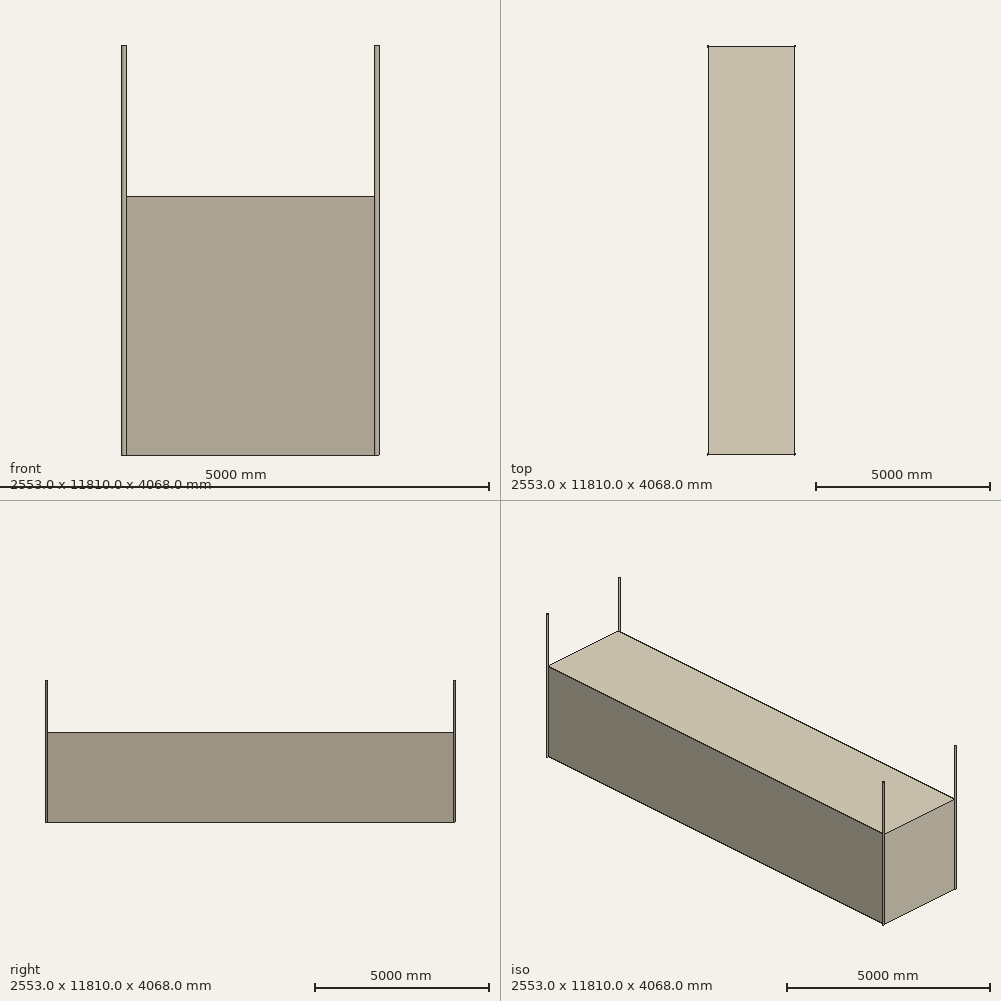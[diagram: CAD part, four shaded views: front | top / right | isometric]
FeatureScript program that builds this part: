
annotation { "Feature Type Name" : "Feature", "Feature Type Description" : "" }
export const myFeature = defineFeature(function(context is Context, id is Id, definition is map)
    precondition{}
    {
        {
            var Q0;
            Q0=qCreatedBy(makeId("Front.planeOp"),FACE);
            var sketch = newSketch(context, id + "F0", { "sketchPlane" : qUnion([Q0])});
            skLineSegment(sketch, "E0.bottom", {"start": v(-1226.5, 1284) * mm, "end": v(1226.5, 1284) * mm});
            skLineSegment(sketch, "E0.top", {"start": v(-1226.5, -1284) * mm, "end": v(1226.5, -1284) * mm});
            skLineSegment(sketch, "E0.left", {"start": v(-1226.5, 1284) * mm, "end": v(-1226.5, -1284) * mm});
            skLineSegment(sketch, "E0.right", {"start": v(1226.5, 1284) * mm, "end": v(1226.5, -1284) * mm});
            skSolve(sketch);
        }
        {
            var Q0;
            Q0=makeQuery(id+"F0.imprint","IMPRINT",FACE,{"disambiguationData":[TD([[makeQuery(id+"F0.imprint","IMPRINT",EDGE,{"derivedFrom":sQuery(id+"F0.wireOp",EDGE,"E0.bottom")}),-1.0]])]});
            extrude(context, id + "F1", {"entities" : qUnion([Q0]), "endBound" : BoundingType.SYMMETRIC, "depth" : 11760 * mm, "offsetDistance" : 25 * mm});
        }
        {
            var Q0;
            Q0=makeQuery(id+"F1.opExtrude","SWEPT_FACE",FACE,{"disambiguationData":[OSD([sQuery(id+"F0.wireOp",EDGE,"E0.right")])]});
            cPlane(context, id + "F2", {"entities" : qUnion([Q0]), "cplaneType" : CPlaneType.OFFSET, "offset" : 25 * mm, "width" : 150 * mm, "height" : 150 * mm});
        }
        {
            var Q0;
            Q0=qCreatedBy(id+"F2.planeOp",FACE);
            var sketch = newSketch(context, id + "F3", { "sketchPlane" : qUnion([Q0])});
            skLineSegment(sketch, "E1", {"start": v(-5880, -1284) * mm, "end": v(-4397.36, 1284) * mm});
            skSolve(sketch);
        }
        {
            var Q0;
            Q0=qCreatedBy(id+"F2.planeOp",FACE);
            var sketch = newSketch(context, id + "F4", { "sketchPlane" : qUnion([Q0])});
            skLineSegment(sketch, "E2", {"start": v(-4397.36, 1284) * mm, "end": v(0, 3822.82) * mm});
            skSolve(sketch);
        }
        {
            var Q0;
            Q0=sQuery(id+"F4.wireOp",EDGE,"E2");
            cPlane(context, id + "F5", {"entities" : qUnion([Q0]), "cplaneType" : CPlaneType.LINE_ANGLE, "offset" : 25 * mm, "angle" : 0 * degree, "width" : 150 * mm, "height" : 150 * mm});
        }
        {
            var Q0;
            Q0=makeQuery(id+"F1.opExtrude","SWEPT_FACE",FACE,{"disambiguationData":[OSD([sQuery(id+"F0.wireOp",EDGE,"E0.top")])]});
            var sketch = newSketch(context, id + "F6", { "sketchPlane" : qUnion([Q0])});
            skCircle(sketch, "E3", {"center": v(1251.5, 5880) * mm, "radius": 25 * mm});
            skSolve(sketch);
        }
        {
            var Q0;
            Q0=qCreatedBy(id+"F2.planeOp",FACE);
            var sketch = newSketch(context, id + "F7", { "sketchPlane" : qUnion([Q0])});
            skLineSegment(sketch, "E4", {"start": v(-5880, 2784) * mm, "end": v(-5880, -1284) * mm});
            skSolve(sketch);
        }
        {
            var Q0;
            Q0=makeQuery(id+"F6.imprint","IMPRINT",FACE,{"disambiguationData":[TD([[makeQuery(id+"F6.imprint","IMPRINT",EDGE,{"derivedFrom":sQuery(id+"F6.wireOp",EDGE,"E3")}),1.0]])]});
            var Q1;
            Q1=sQuery(id+"F7.wireOp",EDGE,"E4");
            sweep(context, id + "F8", {"profiles" : qUnion([Q0]), "path" : qUnion([Q1])});
        }
        {
            var Q0;
            Q0=makeQuery(id+"F8.opSweep","SWEPT_BODY",BODY,{"disambiguationData":[OSD([sQuery(id+"F6.wireOp",EDGE,"E3"),sQuery(id+"F7.wireOp",EDGE,"E4")])]});
            var Q1;
            Q1=qCreatedBy(makeId("Front.planeOp"),FACE);
            mirror(context, id + "F9", {"entities" : qUnion([Q0]), "mirrorPlane" : qUnion([Q1])});
        }
        {
            var Q0;
            Q0=makeQuery(id+"F8.opSweep","SWEPT_BODY",BODY,{"disambiguationData":[OSD([sQuery(id+"F6.wireOp",EDGE,"E3"),sQuery(id+"F7.wireOp",EDGE,"E4")])]});
            var Q1;
            Q1=makeQuery(id+"F9.opPattern","COPY",BODY,{"derivedFrom":makeQuery(id+"F8.opSweep","SWEPT_BODY",BODY,{"disambiguationData":[OSD([sQuery(id+"F6.wireOp",EDGE,"E3"),sQuery(id+"F7.wireOp",EDGE,"E4")])]}),"instanceName":"1"});
            var Q2;
            Q2=qCreatedBy(makeId("Right.planeOp"),FACE);
            mirror(context, id + "F10", {"entities" : qUnion([Q0, Q1]), "mirrorPlane" : qUnion([Q2])});
        }
    });
